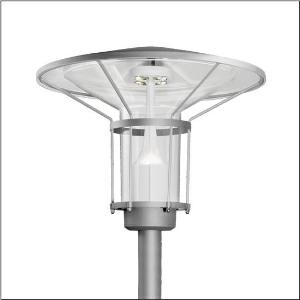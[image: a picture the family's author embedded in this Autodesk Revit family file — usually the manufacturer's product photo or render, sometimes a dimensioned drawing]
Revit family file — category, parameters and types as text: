
# Revit family: laterne_classic_iq___st1_2a_5xa5245kf14h_95b8
name_source: partatom
category: Lighting Fixtures
units: mm (PartAtom-declared; Revit-internal decimal feet)

## family parameters
Cut with Voids When Loaded = No
Host = Face
Light Source = No
Part Type = Normal
Room Calculation Point = No
Round Connector Dimension = Use Diameter
Shared = No

## types (1)
- --- (1 x LED, 1380 lm, 10 W, 4000K)
    Apparent Load = 10 VA
    CIE Flux Codes = 21 60 93 97 100
    Color Rendering = 70
    Color Temperature = 4000K
    Default Elevation = 1800 mm
    Description = Lantern Classic iQ, mast luminaire, Module 540 iQ-SR, primary light control with 3 zone facetted reflector, of plastic, silver coated, highly specular, structured, primary optical cover: cover, of PMMA, transparent, light distribution: ST1.2a, light emission: direct distribution, primary light characteristic: asymmetric, installation type: post-top, LED, High Power LED, rated luminous flux: 1.380lm, luminous efficacy: 138lm/W, light colour: 740, colour temperature: 4000K, control gear: ECG iQ, control: presetting dimming logarithmic, Street-Remote, Auto-Match, Temp-Guard, Lumen-Switch, Night-Set, Smart-Wire, Light-Fading, Desk-Remote (wireless, voltage-free reading and setting of iQ features in the workshop via application-optimized NFC function/RFID function), optimised constant luminous flux control (CLO 2.0), with terminal, 6-pole, max. 2.5mm², mains connection: 230..240V, AC, 50/60Hz, start of lifetime: 10W, end of service life: 10W, reduction: 5W, luminaire housing, upper part, of glass-fibre reinforced polyester, coated, Siteco® metallic grey (DB 702S), diameter: 750mm, height: 596mm, spigot size: d x l = 76 x 70mm (post-top) | with reducer (optional accessory) 60 x 70mm, post-top mast mounting element, of diecast aluminium, coated, Siteco® metallic grey (DB 702S), Module 540 iQ-SR, traffic white (RAL 9016), equipment: standard, protection rating (complete): IP65, insulation class (complete): insulation class II (safety insulation), certification: CE, ENEC, VDE, packaging unit: 1 piece

Light Distribution: ST1.2a
    Height = 596 mm
    Lamp = 1 x LED
    Lamp Light Flux = 1380 lm
    Lamp Power = 10 W
    Lamp count = 1
    Length = 750 mm
    Luminous efficacy = 138 lm/W
    Manufacturer = Siteco
    ModVariant = No
    Model = 5XA5245KF14H
    Number of Poles = 1
    OnlyDefault = Yes
    Power Factor = 1
    Product Name = Laterne Classic iQ | ST1.2a
    Product group = mast luminaire | pylon top
    ProductGroupID = 6100
    Protection Class = Protection class II
    Protection Degree = IP 65
    RLX_Detail_Level = 1
    RLX_Emergency_Light_Flux = 0 lm
    RLX_Emergency_Type = 0
    RLX_Emergency_Type_DB = No
    RlxData = <blob elided: 95705 chars, md5=bbc168d7>
    Socket = socket
    Standby Power = 0 W
    System Light Flux = 1380 lm
    System Power = 10 W
    Type Comments = factory setting: luminous flux: 100 % | dim-lin: 254 | 401 mA
    Type Image = l_1006052.jpg
    URL = http://relux.com
    VarID = @adj_092667
    Voltage = 0 V
    Weight = 0.00 kg
    Width = 0 mm  [stored 0 ft]

note: [stored X ft] marks values corroborated as IEEE doubles in the binary element streams (Revit-internal decimal feet)

## geometry (parser evidence)
native form markers: Blend x4, Sweep x13
no freeform markers — native parametric forms only
